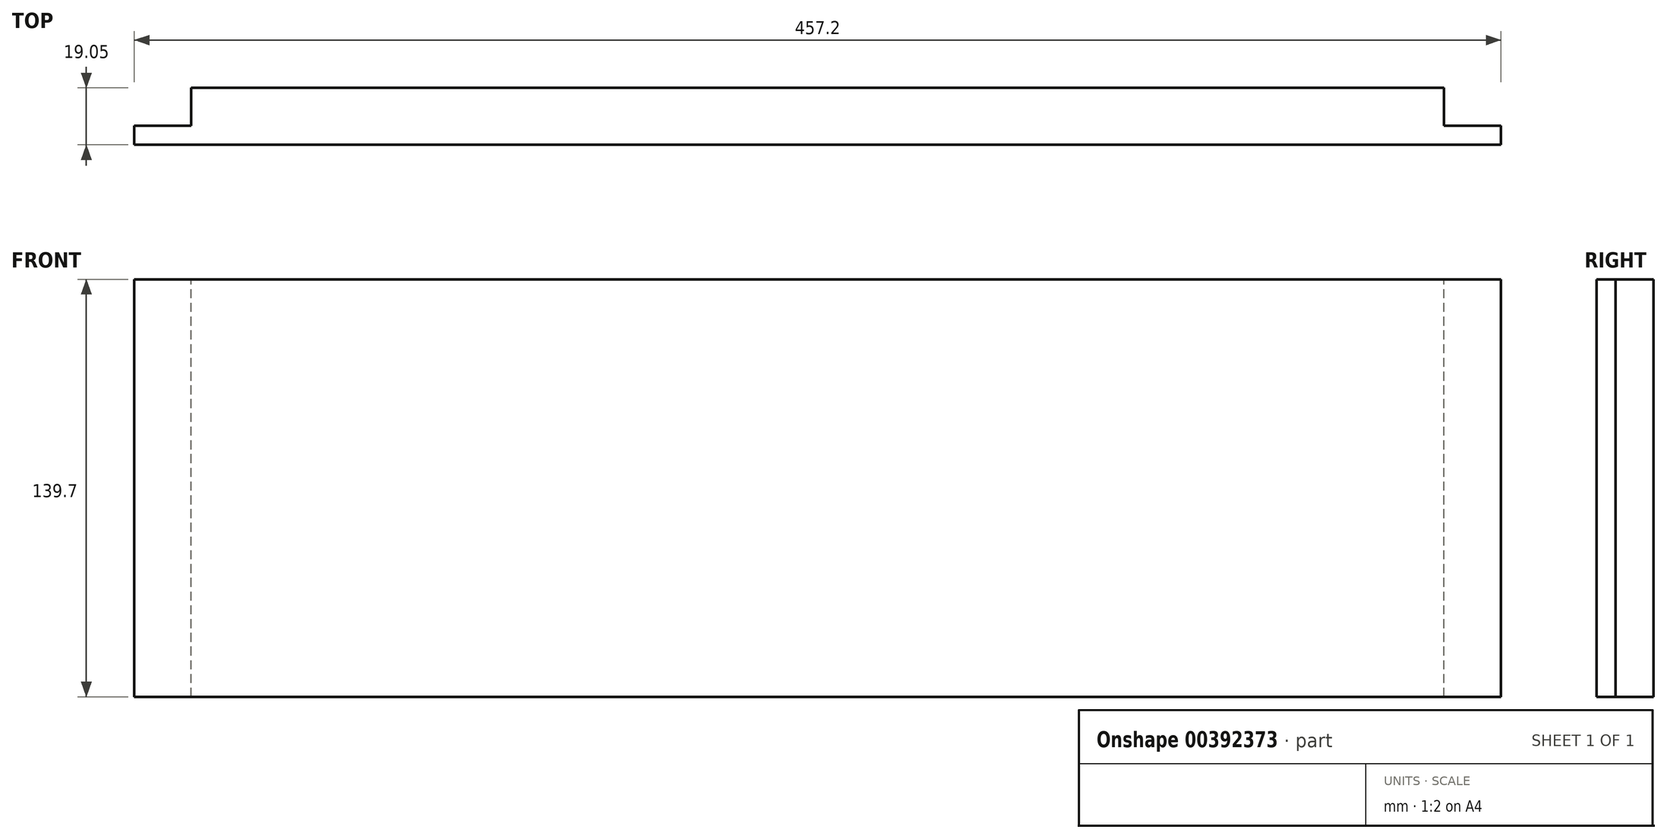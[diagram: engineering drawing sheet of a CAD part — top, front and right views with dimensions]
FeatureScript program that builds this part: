
annotation { "Feature Type Name" : "Feature", "Feature Type Description" : "" }
export const myFeature = defineFeature(function(context is Context, id is Id, definition is map)
    precondition{}
    {
        {
            var Q0;
            Q0=qCreatedBy(makeId("Front.planeOp"),FACE);
            var sketch = newSketch(context, id + "F0", { "sketchPlane" : qUnion([Q0])});
            skLineSegment(sketch, "E0.bottom", {"start": v(0, 0) * mm, "end": v(-457.2, 0) * mm});
            skLineSegment(sketch, "E0.top", {"start": v(0, 139.7) * mm, "end": v(-457.2, 139.7) * mm});
            skLineSegment(sketch, "E0.left", {"start": v(0, 0) * mm, "end": v(0, 139.7) * mm});
            skLineSegment(sketch, "E0.right", {"start": v(-457.2, 0) * mm, "end": v(-457.2, 139.7) * mm});
            skSolve(sketch);
        }
        {
            var Q0;
            Q0=makeQuery(id+"F0.imprint","IMPRINT",FACE,{"disambiguationData":[TD([[makeQuery(id+"F0.imprint","IMPRINT",EDGE,{"derivedFrom":sQuery(id+"F0.wireOp",EDGE,"E0.bottom")}),-1.0]])]});
            extrude(context, id + "F1", {"entities" : qUnion([Q0]), "depth" : 19.05 * mm});
        }
        {
            var Q0;
            Q0=makeQuery(id+"F1.opExtrude","SWEPT_FACE",FACE,{"disambiguationData":[OSD([sQuery(id+"F0.wireOp",EDGE,"E0.top")])]});
            var sketch = newSketch(context, id + "F2", { "sketchPlane" : qUnion([Q0])});
            skLineSegment(sketch, "E1", {"start": v(-19.05, 0) * mm, "end": v(-19.05, -12.7) * mm});
            skLineSegment(sketch, "E2", {"start": v(-19.05, -12.7) * mm, "end": v(0, -12.7) * mm});
            skSolve(sketch);
        }
        {
            var Q0;
            {var subQ0=sQuery(id+"F2.wireOp",EDGE,"E1");Q0=makeQuery(id+"F2.imprint","IMPRINT",FACE,{"disambiguationData":[TD([[makeQuery(id+"F2.imprint","IMPRINT",EDGE,{"derivedFrom":subQ0}),1.0]])]});}
            extrude(context, id + "F3", {"entities" : qUnion([Q0]), "operationType" : NewBodyOperationType.REMOVE, "endBound" : BoundingType.THROUGH_ALL, "oppositeDirection" : true, "depth" : 25.4 * mm});
        }
        {
            var Q0;
            Q0=makeQuery(id+"F1.opExtrude","SWEPT_FACE",FACE,{"disambiguationData":[OSD([sQuery(id+"F0.wireOp",EDGE,"E0.top")])]});
            var sketch = newSketch(context, id + "F4", { "sketchPlane" : qUnion([Q0])});
            skLineSegment(sketch, "E3", {"start": v(-457.2, -12.7) * mm, "end": v(-438.15, -12.7) * mm});
            skLineSegment(sketch, "E4", {"start": v(-438.15, -12.7) * mm, "end": v(-438.15, 0) * mm});
            skSolve(sketch);
        }
        {
            var Q0;
            {var subQ0=sQuery(id+"F4.wireOp",EDGE,"E3");Q0=makeQuery(id+"F4.imprint","IMPRINT",FACE,{"disambiguationData":[TD([[makeQuery(id+"F4.imprint","IMPRINT",EDGE,{"derivedFrom":subQ0}),1.0]])]});}
            extrude(context, id + "F5", {"entities" : qUnion([Q0]), "operationType" : NewBodyOperationType.REMOVE, "endBound" : BoundingType.THROUGH_ALL, "oppositeDirection" : true, "depth" : 25.4 * mm});
        }
    });
